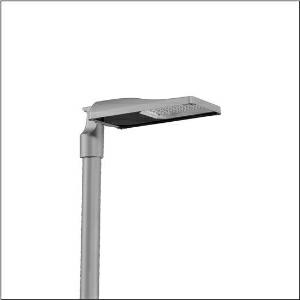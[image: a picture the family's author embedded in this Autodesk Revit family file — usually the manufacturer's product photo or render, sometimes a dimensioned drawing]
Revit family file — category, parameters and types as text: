
# Revit family: streetlight_sl_31_mini___p1_0a_5xh6a31a08ga_6892
name_source: partatom
category: Lighting Fixtures
units: mm (PartAtom-declared; Revit-internal decimal feet)

## family parameters
Cut with Voids When Loaded = No
Host = Face
Light Source = No
Part Type = Normal
Room Calculation Point = No
Round Connector Dimension = Use Diameter
Shared = No

## types (1)
- --- (1 x LED, 5550 lm, 37.3 W, 3000K)
    Apparent Load = 37 VA
    CIE Flux Codes = 23 55 94 100 100
    Color Rendering = 70
    Color Temperature = 3000K
    Default Elevation = 1800 mm
    Description = Streetlight SL 31 mini Easy, Desk-Remote mast luminaire for post-top, side-entry; light control with lens of PMMA; light distribution: P1.0a, direct asymmetric distribution, for standard-compliant lighting for roads and squares; LED: luminous flux: 5.550lm, light colour: 730, colour temperature: 3000K; luminous efficacy: 148,8lm/W; control: pre-setting: linear dimming characteristic, flexible luminous flux parameterisation, time-dependent luminous flux control, constant luminous flux control, intelligent temperature release in ECG and LED module, overheat protection; luminaire housing, of diecast aluminium, Siteco® metallic grey (DB 702S), corrosivity category C5 high according to DIN EN ISO 12944; cover of toughened safety glass, transparent, opened without tools; mast flange of diecast aluminium, Siteco® metallic grey (DB 702S), spigot size: 76/60mm, mast flange included unmounted; with cable H07RN-F 2x 1.5mm², cable length: 6,5m, connection cable pre-assembled; mains connection: 220..240V, AC, 50/60Hz; power consumption (at start of service life): 37,3W / (at end of service life): 38,7W / (with reduced operation 50%): 17,5W; protection rating (complete): IP66; insulation class (complete): insulation class II (safety insulation); impact resistance: IK10; certification: CE, ENEC, ENEC+, VDE, UKCA; permissible operating ambient temperature for outdoor applications: -40..+50°C; packaging unit: 1 piece

Light Distribution: P1.0a
    Height = 76 mm
    Lamp = 1 x LED
    Lamp Light Flux = 5550 lm
    Lamp Power = 37.3 W
    Lamp count = 1
    Length = 547 mm
    Luminous efficacy = 149 lm/W
    Manufacturer = Siteco
    ModVariant = No
    Model = 5XH6A31A08GA
    Number of Poles = 1
    OnlyDefault = Yes
    Power Factor = 1
    Product Name = Streetlight SL 31 mini | P1.0a
    Product group = mast luminaire | pylon top
    ProductGroupID = 6100
    Protection Class = Protection class II
    Protection Degree = IP 66
    RLX_Detail_Level = 1
    RLX_Emergency_Light_Flux = 0 lm
    RLX_Emergency_Type = 0
    RLX_Emergency_Type_DB = No
    RlxData = <blob elided: 39313 chars, md5=e7a9e028>
    Socket = socket
    Standby Power = 0 W
    System Light Flux = 5550 lm
    System Power = 37 W
    Type Comments = factory setting: luminous flux: 100 % | dim-lin: 254 | 386 mA
    Type Image = l_1300326.jpg
    URL = http://relux.com
    VarID = @adj_058290
    Voltage = 0 V
    Weight = 0.00 kg
    Width = 265 mm

## geometry (parser evidence)
native form markers: Blend x4, Sweep x9
no freeform markers — native parametric forms only
